# Revit family: Haworth_Masters_StorageTop_Rectangular
name_source: partatom
category: Furniture Systems
revit_build: Autodesk Revit 2018 (Build: 20170223_1515(x64)
units: mm (PartAtom-declared; Revit-internal decimal feet)

## family parameters
Always vertical = Yes
Cut with Voids When Loaded = No
OmniClass Number = 23.40.70.14.64.21
OmniClass Title = Systems Furniture
Part Type = Normal
Room Calculation Point = No
Round Connector Dimension = Use Diameter
Shared = No
Work Plane-Based = No

## types (7) — shared parameters
Actual Depth = 36 1/8"
Actual Height = 29 5/32"
Assembly Code = E2020200
Custom Size = No
Manufacturer = Haworth
Max. Depth = 36 1/8"
Max. Width = 108"
Min. Depth = 36 1/8"
Min. Width = 60"
Model = XLWT, XZWT
Revision Number = 1
Size = Verify Final Dim. w/ Haworth
Standard Depths = 36 1/8 in.
Standard Widths = 60, 66, 72, 90, 96, 102, 108 in.
Sustainability Info = https://www.haworth.com
URL = www.haworth.com
URL - Product = http://www.haworth.com
Warranty = http://www.haworth.com
Worksurface Thickness = 1 3/16"

## per-type parameters (varying)
| type | Actual Width | Description | Width |
| 36d 108w | 108" | Haworth - Masters - Common Storage Top - 36d 108w | 108" |
| 36d 102w | 102" | Haworth - Masters - Common Storage Top - 36d 102w | 102" |
| 36d 96w | 96" | Haworth - Masters - Common Storage Top - 36d 96w | 96" |
| 36d 90w | 90" | Haworth - Masters - Common Storage Top - 36d 90w | 90" |
| 36d 72w | 72" | Haworth - Masters - Common Storage Top - 36d 72w | 72" |
| 36d 66w | 66" | Haworth - Masters - Common Storage Top - 36d 66w | 66" |
| 36d 60w | 60" | Haworth - Masters - Common Storage Top - 36d 60w | 60" |

## geometry (parser evidence)
native form markers: Sweep x2
no freeform markers — native parametric forms only
